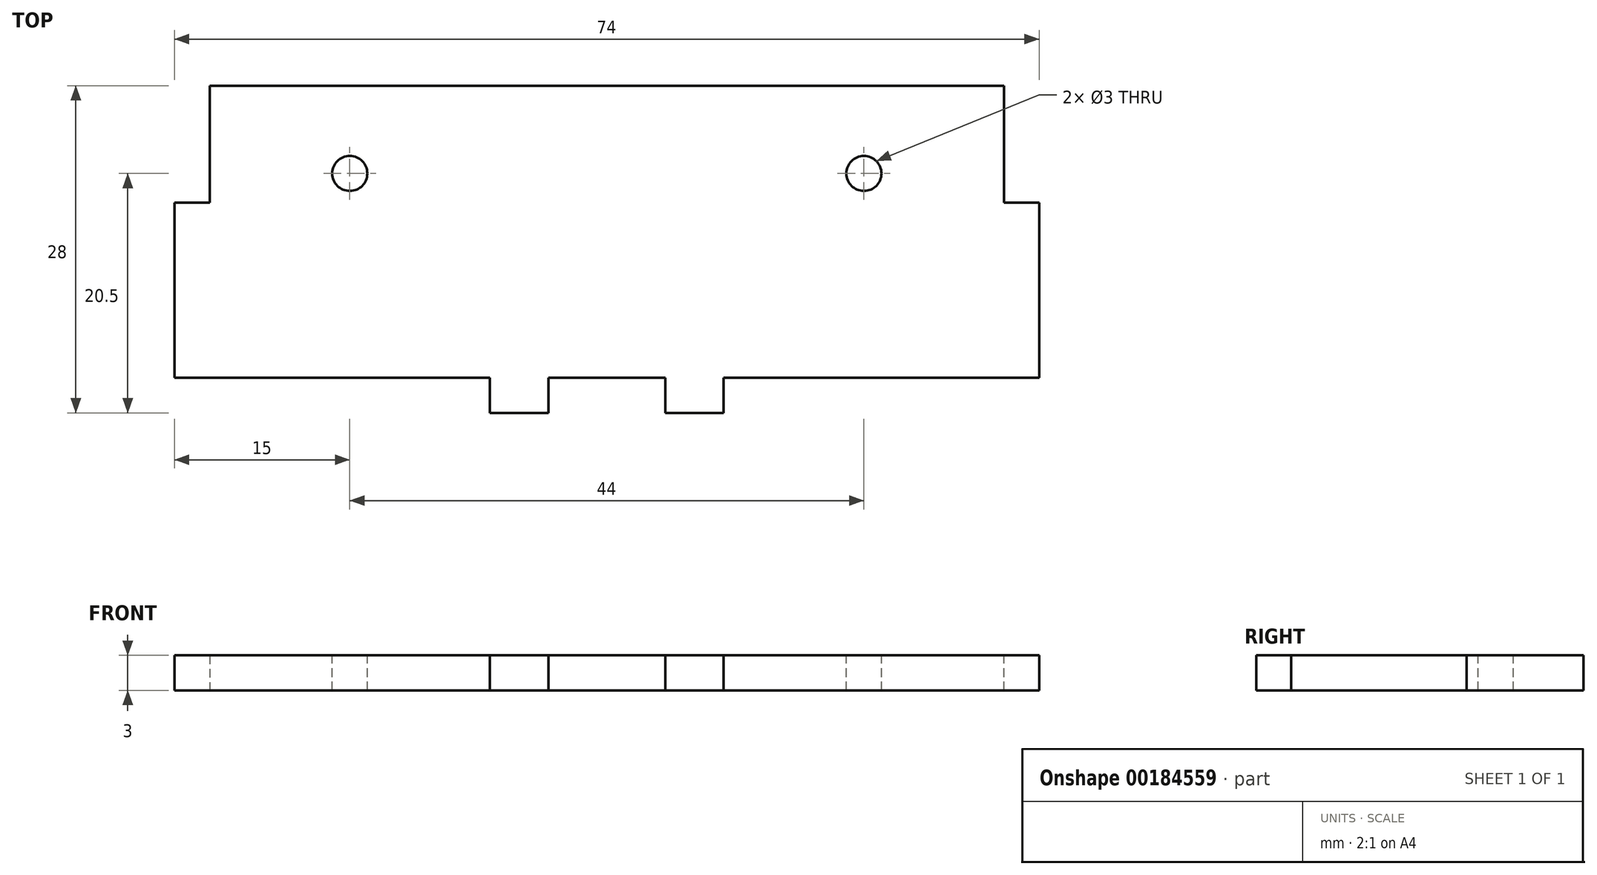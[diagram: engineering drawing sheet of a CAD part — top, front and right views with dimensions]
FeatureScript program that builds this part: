
annotation { "Feature Type Name" : "Feature", "Feature Type Description" : "" }
export const myFeature = defineFeature(function(context is Context, id is Id, definition is map)
    precondition{}
    {
        {
            var Q0;
            Q0=qCreatedBy(makeId("Top.planeOp"),FACE);
            var sketch = newSketch(context, id + "F0", { "sketchPlane" : qUnion([Q0])});
            skLineSegment(sketch, "E0.bottom", {"start": v(34, 12.5) * mm, "end": v(-34, 12.5) * mm});
            skLineSegment(sketch, "E0.top", {"start": v(34, -12.5) * mm, "end": v(-34, -12.5) * mm});
            skLineSegment(sketch, "E0.left", {"start": v(34, 12.5) * mm, "end": v(34, -12.5) * mm});
            skLineSegment(sketch, "E0.right", {"start": v(-34, 12.5) * mm, "end": v(-34, -12.5) * mm});
            skPoint(sketch, "E0.middle", {"position": v(0, 0) * mm});
            skSolve(sketch);
        }
        {
            var Q0;
            Q0=makeQuery(id+"F0.imprint","IMPRINT",FACE,{"disambiguationData":[TD([[makeQuery(id+"F0.imprint","IMPRINT",EDGE,{"derivedFrom":sQuery(id+"F0.wireOp",EDGE,"SoFJLzpH-eIGD-CyFt-csSq-qHylPdstmMme.bottom")}),1.0]])]});
            var Q1;
            Q1=makeQuery(id+"F0.imprint","IMPRINT",FACE,{"disambiguationData":[TD([[makeQuery(id+"F0.imprint","IMPRINT",EDGE,{"derivedFrom":sQuery(id+"F0.wireOp",EDGE,"E0.bottom")}),1.0]])]});
            extrude(context, id + "F1", {"entities" : qUnion([Q0, Q1]), "depth" : 3 * mm});
        }
        {
            var Q0;
            Q0=makeQuery(id+"F1.opExtrude","SWEPT_FACE",FACE,{"disambiguationData":[OSD([sQuery(id+"F0.wireOp",EDGE,"E0.top")])]});
            var sketch = newSketch(context, id + "F2", { "sketchPlane" : qUnion([Q0])});
            skLineSegment(sketch, "E1.bottom", {"start": v(5, 0) * mm, "end": v(10, 0) * mm});
            skLineSegment(sketch, "E1.top", {"start": v(5, 3) * mm, "end": v(10, 3) * mm});
            skLineSegment(sketch, "E1.left", {"start": v(5, 0) * mm, "end": v(5, 3) * mm});
            skLineSegment(sketch, "E1.right", {"start": v(10, 0) * mm, "end": v(10, 3) * mm});
            skSolve(sketch);
        }
        {
            var Q0;
            Q0=makeQuery(id+"F2.imprint","IMPRINT",FACE,{"disambiguationData":[TD([[makeQuery(id+"F2.imprint","IMPRINT",EDGE,{"derivedFrom":sQuery(id+"F2.wireOp",EDGE,"jP9uPcVv-NVQi-ChWz-EsK0-JhAo3QEAKSBN.bottom")}),1.0]])]});
            var Q1;
            Q1=makeQuery(id+"F2.imprint","IMPRINT",FACE,{"disambiguationData":[TD([[makeQuery(id+"F2.imprint","IMPRINT",EDGE,{"derivedFrom":sQuery(id+"F2.wireOp",EDGE,"E1.bottom")}),-1.0]])]});
            extrude(context, id + "F3", {"entities" : qUnion([Q0, Q1]), "operationType" : NewBodyOperationType.ADD, "depth" : 3 * mm});
        }
        {
            var Q0;
            Q0=makeQuery(id+"F1.opExtrude","SWEPT_FACE",FACE,{"disambiguationData":[OSD([sQuery(id+"F0.wireOp",EDGE,"E0.left")])]});
            var sketch = newSketch(context, id + "F4", { "sketchPlane" : qUnion([Q0])});
            skLineSegment(sketch, "E2.bottom", {"start": v(-12.5, 0) * mm, "end": v(2.5, 0) * mm});
            skLineSegment(sketch, "E2.top", {"start": v(-12.5, 3) * mm, "end": v(2.5, 3) * mm});
            skLineSegment(sketch, "E2.left", {"start": v(-12.5, 0) * mm, "end": v(-12.5, 3) * mm});
            skLineSegment(sketch, "E2.right", {"start": v(2.5, 0) * mm, "end": v(2.5, 3) * mm});
            skSolve(sketch);
        }
        {
            var Q0;
            Q0=makeQuery(id+"F4.imprint","IMPRINT",FACE,{"disambiguationData":[TD([[makeQuery(id+"F4.imprint","IMPRINT",EDGE,{"derivedFrom":sQuery(id+"F4.wireOp",EDGE,"E2.bottom")}),-1.0]])]});
            extrude(context, id + "F5", {"entities" : qUnion([Q0]), "operationType" : NewBodyOperationType.ADD, "depth" : 3 * mm});
        }
        {
            var Q0;
            Q0=makeQuery(id+"F1.opExtrude","SWEPT_BODY",BODY,{"disambiguationData":[OSD([sQuery(id+"F0.wireOp",EDGE,"E0.bottom"),sQuery(id+"F0.wireOp",EDGE,"E0.top"),sQuery(id+"F0.wireOp",EDGE,"E0.left"),sQuery(id+"F0.wireOp",EDGE,"E0.right")])]});
            var Q1;
            Q1=qCreatedBy(makeId("Right.planeOp"),FACE);
            mirror(context, id + "F6", {"operationType" : NewBodyOperationType.ADD, "entities" : qUnion([Q0]), "mirrorPlane" : qUnion([Q1])});
        }
        {
            var Q0;
            {var subQ0=makeQuery(id+"F5.boolean.opBoolean","MERGE",FACE,{"derivedFrom":[makeQuery(id+"F3.boolean.opBoolean","MERGE",FACE,{"derivedFrom":[makeQuery(id+"F1.opExtrude","CAP_FACE",FACE,{"disambiguationData":[OSD([sQuery(id+"F0.wireOp",EDGE,"E0.bottom"),sQuery(id+"F0.wireOp",EDGE,"E0.top"),sQuery(id+"F0.wireOp",EDGE,"E0.left"),sQuery(id+"F0.wireOp",EDGE,"E0.right")])],"isStart":false}),makeQuery(id+"F3.opExtrude","SWEPT_FACE",FACE,{"disambiguationData":[OSD([sQuery(id+"F2.wireOp",EDGE,"E1.top")])]})]}),makeQuery(id+"F5.opExtrude","SWEPT_FACE",FACE,{"disambiguationData":[OSD([sQuery(id+"F4.wireOp",EDGE,"E2.top")])]})]});Q0=makeQuery(id+"F6.boolean.opBoolean","MERGE",FACE,{"derivedFrom":[subQ0,makeQuery(id+"F6.opPattern","COPY",FACE,{"derivedFrom":subQ0,"instanceName":"1"})]});}
            var sketch = newSketch(context, id + "F7", { "sketchPlane" : qUnion([Q0])});
            skCircle(sketch, "E3", {"center": v(22, 5) * mm, "radius": 1.5 * mm});
            skCircle(sketch, "E4", {"center": v(-22, 5) * mm, "radius": 1.5 * mm});
            skSolve(sketch);
        }
        {
            var Q0;
            Q0=makeQuery(id+"F7.imprint","IMPRINT",FACE,{"disambiguationData":[TD([[makeQuery(id+"F7.imprint","IMPRINT",EDGE,{"derivedFrom":sQuery(id+"F7.wireOp",EDGE,"E3")}),1.0]])]});
            var Q1;
            Q1=makeQuery(id+"F7.imprint","IMPRINT",FACE,{"disambiguationData":[TD([[makeQuery(id+"F7.imprint","IMPRINT",EDGE,{"derivedFrom":sQuery(id+"F7.wireOp",EDGE,"E4")}),1.0]])]});
            extrude(context, id + "F8", {"entities" : qUnion([Q0, Q1]), "operationType" : NewBodyOperationType.REMOVE, "oppositeDirection" : true, "depth" : 3 * mm});
        }
    });
